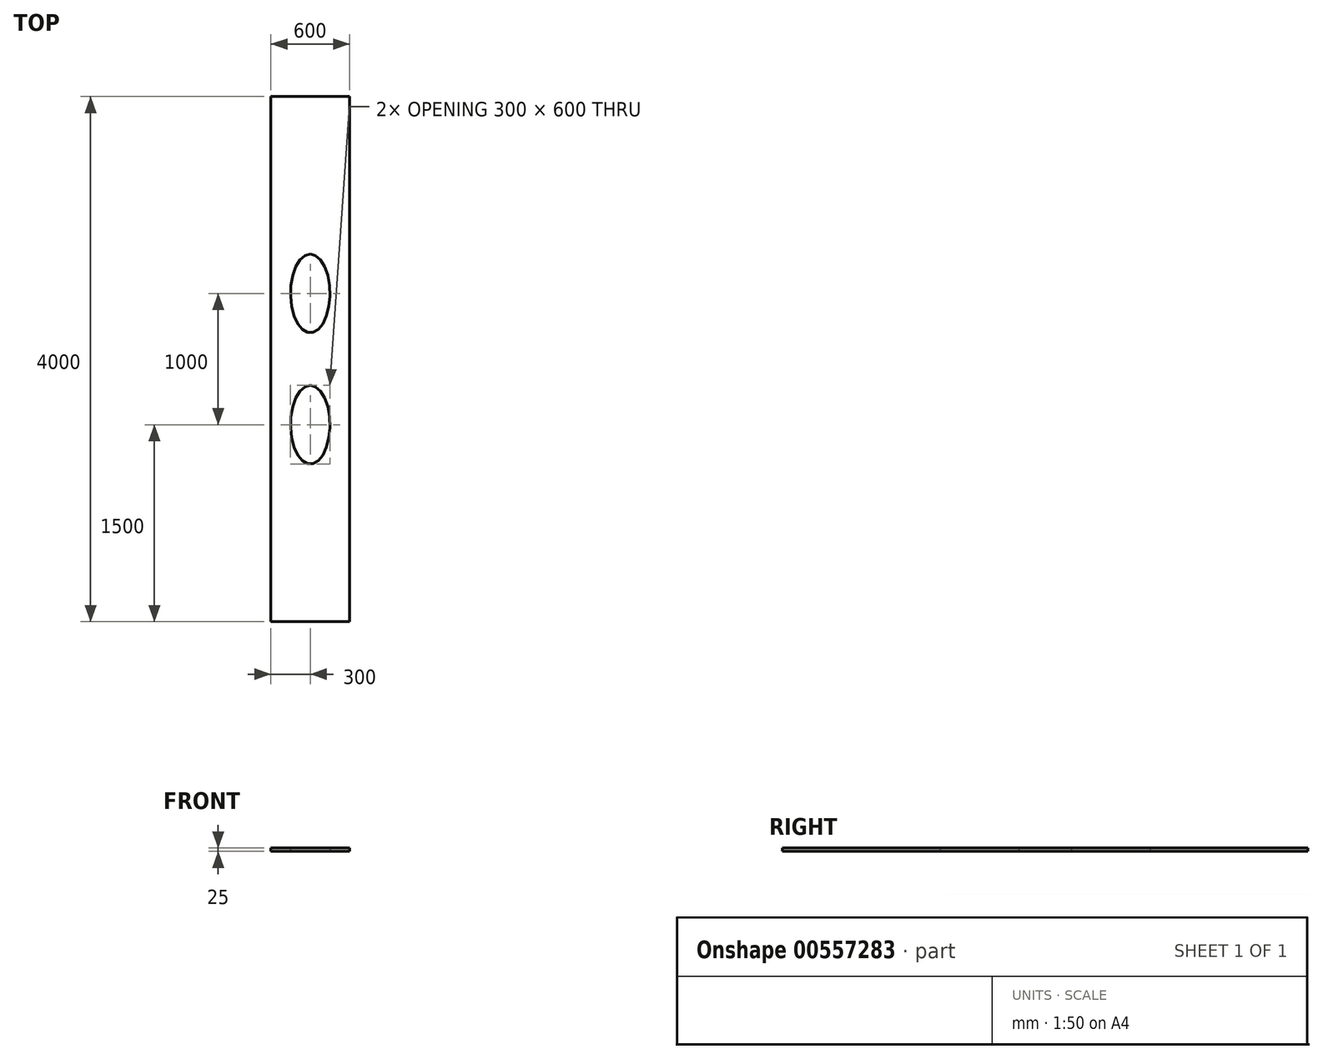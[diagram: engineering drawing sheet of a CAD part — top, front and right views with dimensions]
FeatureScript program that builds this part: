
annotation { "Feature Type Name" : "Feature", "Feature Type Description" : "" }
export const myFeature = defineFeature(function(context is Context, id is Id, definition is map)
    precondition{}
    {
        {
            var Q0;
            Q0=qCreatedBy(makeId("Top.planeOp"),FACE);
            var sketch = newSketch(context, id + "F0", { "sketchPlane" : qUnion([Q0])});
            skLineSegment(sketch, "E0.bottom", {"start": v(0, 0) * mm, "end": v(600, 0) * mm});
            skLineSegment(sketch, "E0.top", {"start": v(0, 4000) * mm, "end": v(600, 4000) * mm});
            skLineSegment(sketch, "E0.left", {"start": v(0, 0) * mm, "end": v(0, 4000) * mm});
            skLineSegment(sketch, "E0.right", {"start": v(600, 0) * mm, "end": v(600, 4000) * mm});
            skArc(sketch, "E1", {"start": v(600, 486.54) * mm, "mid": v(450, 336.54) * mm, "end": v(600, 186.54) * mm});
            skArc(sketch, "E2", {"start": v(600, 883.94) * mm, "mid": v(450, 733.94) * mm, "end": v(600, 583.94) * mm});
            skEllipse(sketch, "E3", {"center": v(300, 1500) * mm, "majorRadius": 300 * mm, "minorRadius": 150 * mm, "majorAxis": v(0, 1)});
            skPoint(sketch, "E4", {"position": v(300, 1800) * mm});
            skEllipse(sketch, "E5", {"center": v(300, 2500) * mm, "majorRadius": 300 * mm, "minorRadius": 150 * mm, "majorAxis": v(0, 1)});
            skLineSegment(sketch, "E6", {"start": v(0, 3100) * mm, "end": v(150, 3100) * mm});
            skArc(sketch, "E7", {"start": v(150, 2900) * mm, "mid": v(250, 3000) * mm, "end": v(150, 3100) * mm});
            skArc(sketch, "E8", {"start": v(150, 2900) * mm, "mid": v(79.29, 2929.29) * mm, "end": v(50, 3000) * mm});
            skLineSegment(sketch, "E9", {"start": v(50, 3000) * mm, "end": v(0, 3000) * mm});
            skSolve(sketch);
        }
        {
            var Q0;
            {var subQ4=sQuery(id+"F0.wireOp",EDGE,"E0.bottom");Q0=makeQuery(id+"F0.imprint","IMPRINT",FACE,{"disambiguationData":[TD([[makeQuery(id+"F0.imprint","IMPRINT",EDGE,{"derivedFrom":subQ4}),1.0]])]});}
            var Q1;
            {var subQ0=sQuery(id+"F0.wireOp",EDGE,"E6");Q1=makeQuery(id+"F0.imprint","IMPRINT",FACE,{"disambiguationData":[TD([[makeQuery(id+"F0.imprint","IMPRINT",EDGE,{"derivedFrom":subQ0}),-1.0]])]});}
            var Q2;
            {var subQ0=sQuery(id+"F0.wireOp",EDGE,"E2");Q2=makeQuery(id+"F0.imprint","IMPRINT",FACE,{"disambiguationData":[TD([[makeQuery(id+"F0.imprint","IMPRINT",EDGE,{"derivedFrom":subQ0}),1.0]])]});}
            var Q3;
            {var subQ0=sQuery(id+"F0.wireOp",EDGE,"E1");Q3=makeQuery(id+"F0.imprint","IMPRINT",FACE,{"disambiguationData":[TD([[makeQuery(id+"F0.imprint","IMPRINT",EDGE,{"derivedFrom":subQ0}),1.0]])]});}
            extrude(context, id + "F1", {"entities" : qUnion([Q0, Q1, Q2, Q3]), "depth" : 25 * mm, "offsetDistance" : 25 * mm});
        }
    });
